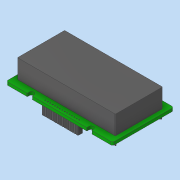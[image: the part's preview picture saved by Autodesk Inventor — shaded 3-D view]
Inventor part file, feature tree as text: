
AUTODESK INVENTOR PART (.ipt)
format: ipt  version: 2018 (Build 220112000, 112)  size: 359,936 bytes
history: native  units: mm
features: sketch x6, extrude x5, pattern_linear x2, hole x1, fillet x1, projected_geometry x1
ambient origin geometry x8: Origin, YZ Plane, XZ Plane, XY Plane, X Axis, Y Axis, Z Axis, Center Point
bodies: Volumenkörper1 (feature_tree)
feature tree (16):
  extrude  "Extrusion1"  Depth=32.0mm
  extrude  "Extrusion2"  Depth=2.5mm
  hole  "Bohrung1"  [1 undecoded]
  pattern_linear  "Rechteckige Anordnung1"  Spacing1=1.0mm  [1 undecoded]
  extrude  "Extrusion3"  Depth=4.57mm
  extrude  "Extrusion4"  Depth=2.5mm
  extrude  "Extrusion5"  Depth=1.6mm TaperAngle=0.0deg
  pattern_linear  "Rechteckige Anordnung2"  Spacing1=18.96mm  [1 undecoded]
  fillet  "Rundung1"  Radius=1.5mm
  sketch  "Skizze1"  dims[d0=55.7mm d1=32.0mm]
  sketch  "Skizze2"  dims[d6=1.6mm d7=0.0mm d8=2.5mm]
  sketch  "Skizze3"  dims[d9=12.25mm d10=1.25mm]
  sketch  "Skizze4"  dims[d11=1.0mm]
  sketch  "Skizze5"  dims[d12=2.5mm d13=1.25mm d14=1.0mm d15=31.2mm]
  projected_geometry  "Projizierte Kontur1"
  sketch  "Skizze6"  dims[d19=2.5mm d20=1.0mm d21=12.25mm d22=2.5mm d23=1.0mm d24=31.2mm d25=1.6mm d26=0.0mm d27=18.96mm d28=1.5mm d29=0.5mm d30=6.0mm d31=4.0mm d32=2.0mm d33=90.0deg d34=8.0mm d35=20.594885mm d36=150.0mm d38=1.27mm d39=1.0mm d40=0.2mm d41=51.3mm d42=24.7mm d43=9.9mm d44=0.0mm d45=6.0mm d46=0.5mm d47=45.0deg d48=0.353553mm d49=0.353553mm d50=6.0mm d51=45.0deg d52=45.0deg d55=3.0mm d56=0.0mm d57=1.27mm d58=1.27mm d59=0.635mm d60=2.54mm d61=90.0deg d62=0.635mm d63=2.54mm d64=0.635mm d65=45.0deg d66=0.25mm d67=45.0deg d68=0.25mm d69=0.25mm d70=45.0deg d71=45.0deg d72=0.25mm d73=4.57mm d74=0.0mm d75=150.0mm d77=1.27mm]
note: 3 required parameter values undecoded (feature->parameter linkage not recoverable at this tier; creation-order binding heuristic only, values carry confidence <= 0.55)
